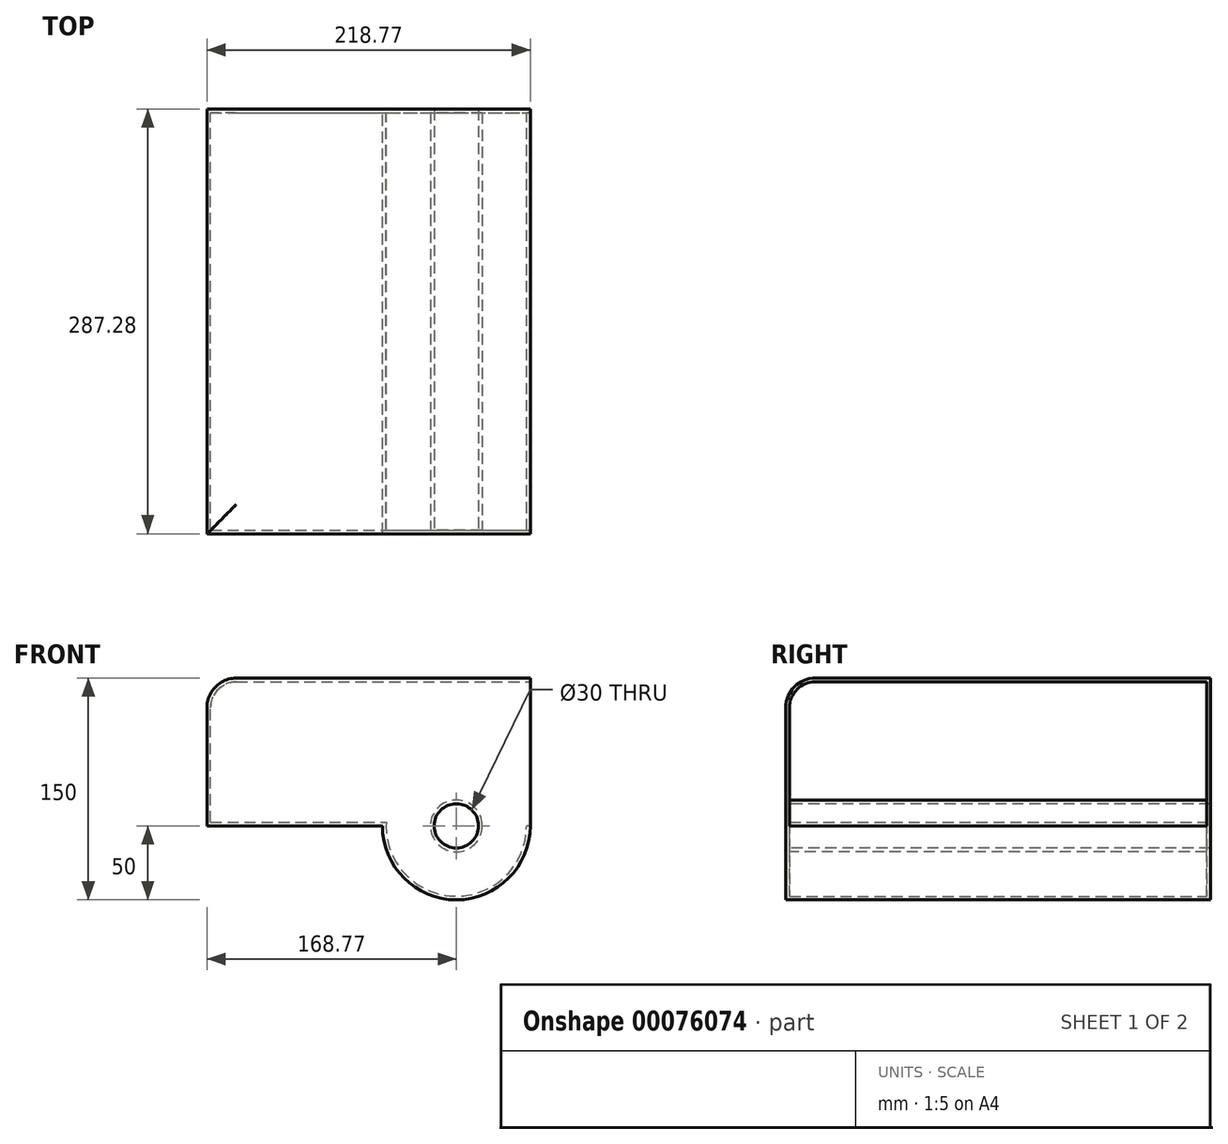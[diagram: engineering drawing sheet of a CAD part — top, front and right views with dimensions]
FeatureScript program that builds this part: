
annotation { "Feature Type Name" : "Feature", "Feature Type Description" : "" }
export const myFeature = defineFeature(function(context is Context, id is Id, definition is map)
    precondition{}
    {
        {
            var Q0;
            Q0=qCreatedBy(makeId("Front.planeOp"),FACE);
            var sketch = newSketch(context, id + "F0", { "sketchPlane" : qUnion([Q0])});
            skLineSegment(sketch, "E0", {"start": v(-50, 0) * mm, "end": v(-50, 100) * mm});
            skLineSegment(sketch, "E1", {"start": v(-50, 100) * mm, "end": v(50, 100) * mm});
            skLineSegment(sketch, "E2", {"start": v(50, 100) * mm, "end": v(50, 0) * mm});
            skArc(sketch, "E3", {"start": v(-50, 0) * mm, "mid": v(0, -50) * mm, "end": v(50, 0) * mm});
            skSolve(sketch);
        }
        {
            var Q0;
            Q0=makeQuery(id+"F0.imprint","IMPRINT",FACE,{"disambiguationData":[TD([[makeQuery(id+"F0.imprint","IMPRINT",EDGE,{"derivedFrom":sQuery(id+"F0.wireOp",EDGE,"E0")}),-1.0]])]});
            extrude(context, id + "F1", {"entities" : qUnion([Q0]), "depth" : 150 * mm});
        }
        {
            var Q0;
            Q0=makeQuery(id+"F1.opExtrude","CAP_FACE",FACE,{"disambiguationData":[OSD([sQuery(id+"F0.wireOp",EDGE,"E0"),sQuery(id+"F0.wireOp",EDGE,"E1"),sQuery(id+"F0.wireOp",EDGE,"E2"),sQuery(id+"F0.wireOp",EDGE,"E3")])],"isStart":false});
            var sketch = newSketch(context, id + "F2", { "sketchPlane" : qUnion([Q0])});
            skCircle(sketch, "E4", {"center": v(0, 0) * mm, "radius": 15 * mm});
            skSolve(sketch);
        }
        {
            var Q0;
            Q0 = qSketchRegion(id + "F2", true);
            extrude(context, id + "F3", {"entities" : qUnion([Q0]), "operationType" : NewBodyOperationType.REMOVE, "endBound" : BoundingType.THROUGH_ALL, "oppositeDirection" : true, "depth" : 25 * mm});
        }
        {
            var Q0;
            Q0=makeQuery(id+"F1.opExtrude","CAP_FACE",FACE,{"disambiguationData":[OSD([sQuery(id+"F0.wireOp",EDGE,"E0"),sQuery(id+"F0.wireOp",EDGE,"E1"),sQuery(id+"F0.wireOp",EDGE,"E2"),sQuery(id+"F0.wireOp",EDGE,"E3")])],"isStart":false});
            extrude(context, id + "F4", {"entities" : qUnion([Q0]), "operationType" : NewBodyOperationType.ADD, "depth" : 137.28 * mm});
        }
        {
            var Q0;
            {var subQ0=sQuery(id+"F0.wireOp",EDGE,"E0");Q0=makeQuery(id+"F4.boolean.opBoolean","MERGE",FACE,{"derivedFrom":[makeQuery(id+"F1.opExtrude","SWEPT_FACE",FACE,{"disambiguationData":[OSD([subQ0])]}),makeQuery(id+"F4.opExtrude","SWEPT_FACE",FACE,{"disambiguationData":[OSD([subQ0])]})]});}
            extrude(context, id + "F5", {"entities" : qUnion([Q0]), "operationType" : NewBodyOperationType.ADD, "depth" : 118.77 * mm});
        }
        {
            var Q0;
            {var subQ0=sQuery(id+"F0.wireOp",EDGE,"E1");var subQ1=sQuery(id+"F0.wireOp",EDGE,"E0");Q0=makeQuery(id+"F5.boolean.opBoolean","MERGE",EDGE,{"derivedFrom":[makeQuery(id+"F4.opExtrude","CAP_EDGE",EDGE,{"disambiguationData":[OSD([subQ0])],"isStart":false}),makeQuery(id+"F5.opExtrude","SWEPT_EDGE",EDGE,{"disambiguationData":[OSD([subQ1,subQ0]),TDD([makeQuery(id+"F4.opExtrude","CAP_VERTEX",VERTEX,{"disambiguationData":[OSD([subQ1,subQ0])],"isStart":false})])]})]});}
            var Q1;
            Q1=makeQuery(id+"F5.opExtrude","CAP_EDGE",EDGE,{"disambiguationData":[OSD([sQuery(id+"F0.wireOp",EDGE,"E0"),sQuery(id+"F0.wireOp",EDGE,"E1")])],"isStart":false});
            fillet(context, id + "F6", {"entities" : qUnion([Q0, Q1]), "radius" : 20 * mm, "tangentPropagation" : true, "allowEdgeOverflow" : false});
        }
        {
            var Q0;
            {var subQ0=sQuery(id+"F0.wireOp",EDGE,"E2");Q0=makeQuery(id+"F4.boolean.opBoolean","MERGE",FACE,{"derivedFrom":[makeQuery(id+"F1.opExtrude","SWEPT_FACE",FACE,{"disambiguationData":[OSD([subQ0])]}),makeQuery(id+"F4.opExtrude","SWEPT_FACE",FACE,{"disambiguationData":[OSD([subQ0])]})]});}
            shell(context, id + "F7", {"entities" : qUnion([Q0]), "thickness" : 2.5 * mm});
        }
    });
